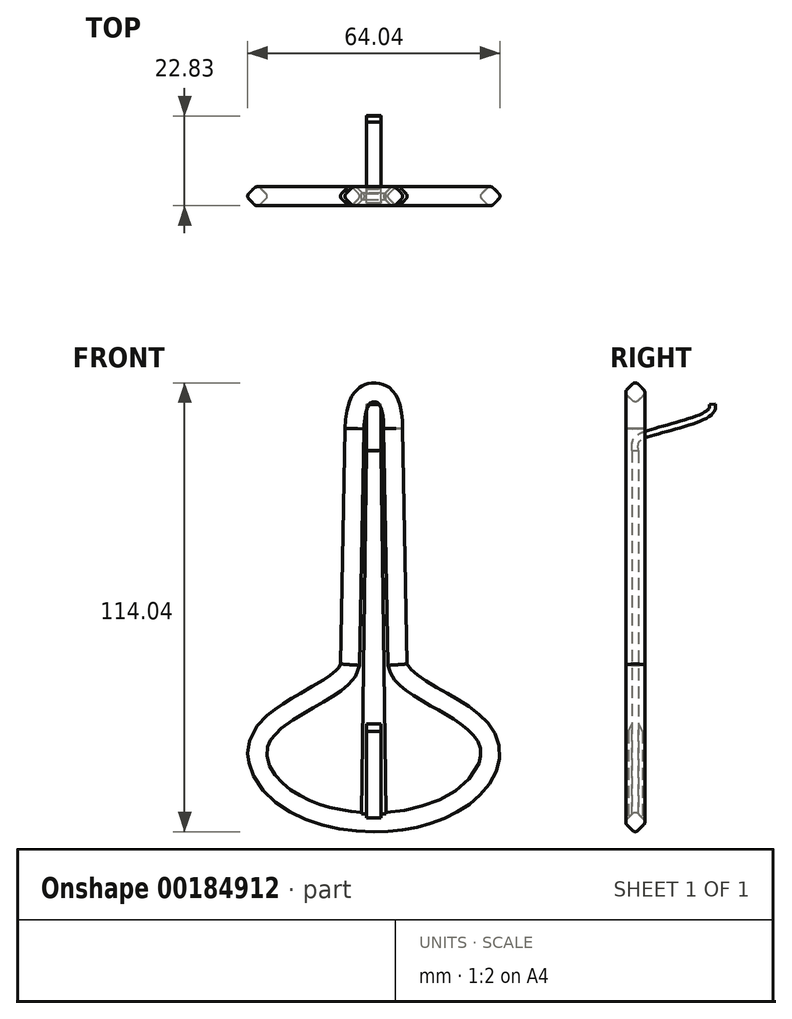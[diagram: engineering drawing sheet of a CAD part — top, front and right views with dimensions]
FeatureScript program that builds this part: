
annotation { "Feature Type Name" : "Feature", "Feature Type Description" : "" }
export const myFeature = defineFeature(function(context is Context, id is Id, definition is map)
    precondition{}
    {
        {
            var Q0;
            Q0=qCreatedBy(makeId("Front.planeOp"),FACE);
            var sketch = newSketch(context, id + "F0", { "sketchPlane" : qUnion([Q0])});
            skLineSegment(sketch, "E0.bottom", {"start": v(0, 0) * mm, "end": v(30, 0) * mm, "construction": true});
            skLineSegment(sketch, "E0.top", {"start": v(0, 100) * mm, "end": v(30, 100) * mm, "construction": true});
            skLineSegment(sketch, "E0.left", {"start": v(0, 0) * mm, "end": v(0, 100) * mm, "construction": true});
            skLineSegment(sketch, "E0.right", {"start": v(30, 0) * mm, "end": v(30, 100) * mm, "construction": true});
            skLineSegment(sketch, "E1", {"start": v(4.9, 100) * mm, "end": v(6.05, 40.01) * mm});
            skFitSpline(sketch, "E2", {"points": [v(6.05, 40.01) * mm, v(28.58, 21.64) * mm, v(0, 0) * mm], "startDerivative": vector(4.45, -38.4) * mm, "endDerivative": vector(-122.64, 0) * mm});
            skSolve(sketch);
        }
        {
            var Q0;
            Q0=sQuery(id+"F0.wireOp",VERTEX,"E2.2.internal");
            var Q1;
            Q1=qCreatedBy(makeId("Right.planeOp"),FACE);
            cPlane(context, id + "F1", {"entities" : qUnion([Q0, Q1]), "cplaneType" : CPlaneType.PLANE_POINT, "offset" : 25 * mm, "width" : 150 * mm, "height" : 150 * mm});
        }
        {
            var Q0;
            Q0=qCreatedBy(id+"F1.planeOp",FACE);
            var sketch = newSketch(context, id + "F2", { "sketchPlane" : qUnion([Q0])});
            skCircle(sketch, "E3.cCircle", {"center": v(0, 0) * mm, "radius": 2 * mm, "construction": true});
            skLineSegment(sketch, "E3.0", {"start": v(-2.12, 0.7) * mm, "end": v(-0.7, 2.12) * mm});
            skLineSegment(sketch, "E3.1", {"start": v(0.7, 2.12) * mm, "end": v(2.12, 0.7) * mm});
            skLineSegment(sketch, "E3.2", {"start": v(2.12, -0.7) * mm, "end": v(0.7, -2.12) * mm});
            skLineSegment(sketch, "E3.3", {"start": v(-0.7, -2.12) * mm, "end": v(-2.12, -0.7) * mm});
            skPoint(sketch, "E3.0.midPoint", {"position": v(0, 2) * mm});
            skPoint(sketch, "E4.visualSharp", {"position": v(0, 2.83) * mm});
            skArc(sketch, "E4.filletArc", {"start": v(0.7, 2.12) * mm, "mid": v(0, 2.41) * mm, "end": v(-0.7, 2.12) * mm});
            skPoint(sketch, "E5.visualSharp", {"position": v(-2.83, 0) * mm});
            skArc(sketch, "E5.filletArc", {"start": v(-2.12, 0.7) * mm, "mid": v(-2.41, 0) * mm, "end": v(-2.12, -0.7) * mm});
            skPoint(sketch, "E6.visualSharp", {"position": v(0, -2.83) * mm});
            skArc(sketch, "E6.filletArc", {"start": v(-0.7, -2.12) * mm, "mid": v(0, -2.41) * mm, "end": v(0.7, -2.12) * mm});
            skPoint(sketch, "E7.visualSharp", {"position": v(2.83, 0) * mm});
            skArc(sketch, "E7.filletArc", {"start": v(2.12, -0.7) * mm, "mid": v(2.41, 0) * mm, "end": v(2.12, 0.7) * mm});
            skSolve(sketch);
        }
        {
            var Q0;
            Q0=makeQuery(id+"F2.imprint","IMPRINT",FACE,{"disambiguationData":[TD([[makeQuery(id+"F2.imprint","IMPRINT",EDGE,{"derivedFrom":sQuery(id+"F2.wireOp",EDGE,"E3.0")}),-1.0]])]});
            var Q1;
            Q1=sQuery(id+"F0.wireOp",EDGE,"E2");
            var Q2;
            Q2=sQuery(id+"F0.wireOp",EDGE,"E1");
            sweep(context, id + "F3", {"profiles" : qUnion([Q0]), "path" : qUnion([Q1, Q2])});
        }
        {
            var Q0;
            Q0=makeQuery(id+"F3.opSweep","SWEPT_BODY",BODY,{"disambiguationData":[OSD([sQuery(id+"F0.wireOp",EDGE,"E1"),sQuery(id+"F2.wireOp",EDGE,"E3.0"),sQuery(id+"F2.wireOp",EDGE,"E3.1"),sQuery(id+"F2.wireOp",EDGE,"E3.2"),sQuery(id+"F2.wireOp",EDGE,"E3.3"),sQuery(id+"F2.wireOp",EDGE,"E4.filletArc"),sQuery(id+"F2.wireOp",EDGE,"E5.filletArc"),sQuery(id+"F2.wireOp",EDGE,"E6.filletArc"),sQuery(id+"F2.wireOp",EDGE,"E7.filletArc")])]});
            var Q1;
            Q1=qCreatedBy(makeId("Right.planeOp"),FACE);
            mirror(context, id + "F4", {"operationType" : NewBodyOperationType.ADD, "entities" : qUnion([Q0]), "mirrorPlane" : qUnion([Q1])});
        }
        {
            var Q0;
            Q0=qCreatedBy(makeId("Front.planeOp"),FACE);
            var sketch = newSketch(context, id + "F5", { "sketchPlane" : qUnion([Q0])});
            skLineSegment(sketch, "E8", {"start": v(1.82, 94.4) * mm, "end": v(3.15, 0) * mm});
            skLineSegment(sketch, "E9", {"start": v(0, 0) * mm, "end": v(0, 122.08) * mm, "construction": true});
            skLineSegment(sketch, "E10.MirrorCS", {"start": v(-1.82, 94.4) * mm, "end": v(-3.15, 0) * mm});
            skLineSegment(sketch, "E11", {"start": v(-1.82, 94.4) * mm, "end": v(1.82, 94.4) * mm});
            skLineSegment(sketch, "E12", {"start": v(-3.15, 0) * mm, "end": v(3.15, 0) * mm});
            skSolve(sketch);
        }
        {
            var Q0;
            Q0 = qSketchRegion(id + "F5", true);
            extrude(context, id + "F6", {"entities" : qUnion([Q0]), "endBound" : BoundingType.SYMMETRIC, "depth" : 1.6 * mm});
        }
        {
            var Q0;
            Q0=qCreatedBy(makeId("Right.planeOp"),FACE);
            var sketch = newSketch(context, id + "F7", { "sketchPlane" : qUnion([Q0])});
            skFitSpline(sketch, "E13", {"points": [v(0, 94.22) * mm, v(2.77, 98.58) * mm, v(17.87, 103.42) * mm, v(19.56, 106.16) * mm], "startDerivative": vector(-4.31, 31.5) * mm, "endDerivative": vector(-3, 14.7) * mm});
            skSolve(sketch);
        }
        {
            var Q0;
            Q0=makeQuery(id+"F6.opExtrude","SWEPT_FACE",FACE,{"disambiguationData":[OSD([sQuery(id+"F5.wireOp",EDGE,"E11")])]});
            var Q1;
            Q1=sQuery(id+"F7.wireOp",EDGE,"E13");
            sweep(context, id + "F8", {"operationType" : NewBodyOperationType.ADD, "profiles" : qUnion([Q0]), "path" : qUnion([Q1])});
        }
        {
            var Q0;
            Q0=qCreatedBy(makeId("Front.planeOp"),FACE);
            var sketch = newSketch(context, id + "F9", { "sketchPlane" : qUnion([Q0])});
            skPoint(sketch, "E14.0", {"position": v(-4.9, 100) * mm});
            skPoint(sketch, "E15.0", {"position": v(4.9, 100) * mm});
            skFitSpline(sketch, "E16", {"points": [v(-4.9, 100) * mm, v(0, 109.2) * mm, v(4.9, 100) * mm], "startDerivative": vector(1, 44.01) * mm, "endDerivative": vector(-0.51, -45.62) * mm});
            skSolve(sketch);
        }
        {
            var Q0;
            Q0=makeQuery(id+"F4.opPattern","COPY",FACE,{"derivedFrom":makeQuery(id+"F3.opSweep","CAP_FACE",FACE,{"disambiguationData":[OSD([sQuery(id+"F0.wireOp",VERTEX,"E1.start"),sQuery(id+"F2.wireOp",EDGE,"E3.0"),sQuery(id+"F2.wireOp",EDGE,"E3.1"),sQuery(id+"F2.wireOp",EDGE,"E3.2"),sQuery(id+"F2.wireOp",EDGE,"E3.3"),sQuery(id+"F2.wireOp",EDGE,"E4.filletArc"),sQuery(id+"F2.wireOp",EDGE,"E5.filletArc"),sQuery(id+"F2.wireOp",EDGE,"E6.filletArc"),sQuery(id+"F2.wireOp",EDGE,"E7.filletArc")])],"isStart":false}),"instanceName":"1"});
            var Q1;
            Q1 = qConstructionFilter(qBodyType(qCreatedBy(id + "F9" ,EDGE), BodyType.WIRE), ConstructionObject.NO);
            sweep(context, id + "F10", {"profiles" : qUnion([Q0]), "path" : qUnion([Q1])});
        }
        {
            var Q0;
            Q0=qCreatedBy(makeId("Top.planeOp"),FACE);
            var sketch = newSketch(context, id + "F11", { "sketchPlane" : qUnion([Q0])});
            skLineSegment(sketch, "E17.0", {"start": v(-1.82, -0.8) * mm, "end": v(1.82, -0.8) * mm});
            skLineSegment(sketch, "E18.0", {"start": v(-1.82, 0.8) * mm, "end": v(1.82, 0.8) * mm});
            skLineSegment(sketch, "E19.0", {"start": v(-1.82, 1.8) * mm, "end": v(1.82, 1.8) * mm});
            skLineSegment(sketch, "E20.0", {"start": v(-1.82, -1.8) * mm, "end": v(1.82, -1.8) * mm});
            skLineSegment(sketch, "E21", {"start": v(1.82, 1.8) * mm, "end": v(1.82, -1.8) * mm});
            skLineSegment(sketch, "E22", {"start": v(-1.82, 1.8) * mm, "end": v(-1.82, -1.8) * mm});
            skSolve(sketch);
        }
        {
            var Q0;
            Q0 = qSketchRegion(id + "F11", true);
            extrude(context, id + "F12", {"entities" : qUnion([Q0]), "operationType" : NewBodyOperationType.ADD, "depth" : 25 * mm});
        }
        {
            var Q0;
            Q0=makeQuery(id+"F12.opExtrude","CAP_EDGE",EDGE,{"disambiguationData":[OSD([sQuery(id+"F11.wireOp",EDGE,"E19.0")])],"isStart":false});
            chamfer(context, id + "F13", {"entities" : qUnion([Q0]), "chamferType" : ChamferType.TWO_OFFSETS, "width1" : 1 * mm, "oppositeDirection" : true, "width2" : 2 * mm});
        }
        {
            var Q0;
            Q0=makeQuery(id+"F12.opExtrude","CAP_EDGE",EDGE,{"disambiguationData":[OSD([sQuery(id+"F11.wireOp",EDGE,"E20.0")])],"isStart":false});
            chamfer(context, id + "F14", {"entities" : qUnion([Q0]), "chamferType" : ChamferType.TWO_OFFSETS, "width1" : 1 * mm, "oppositeDirection" : false, "width2" : 2 * mm, "tangentPropagation" : true});
        }
    });
